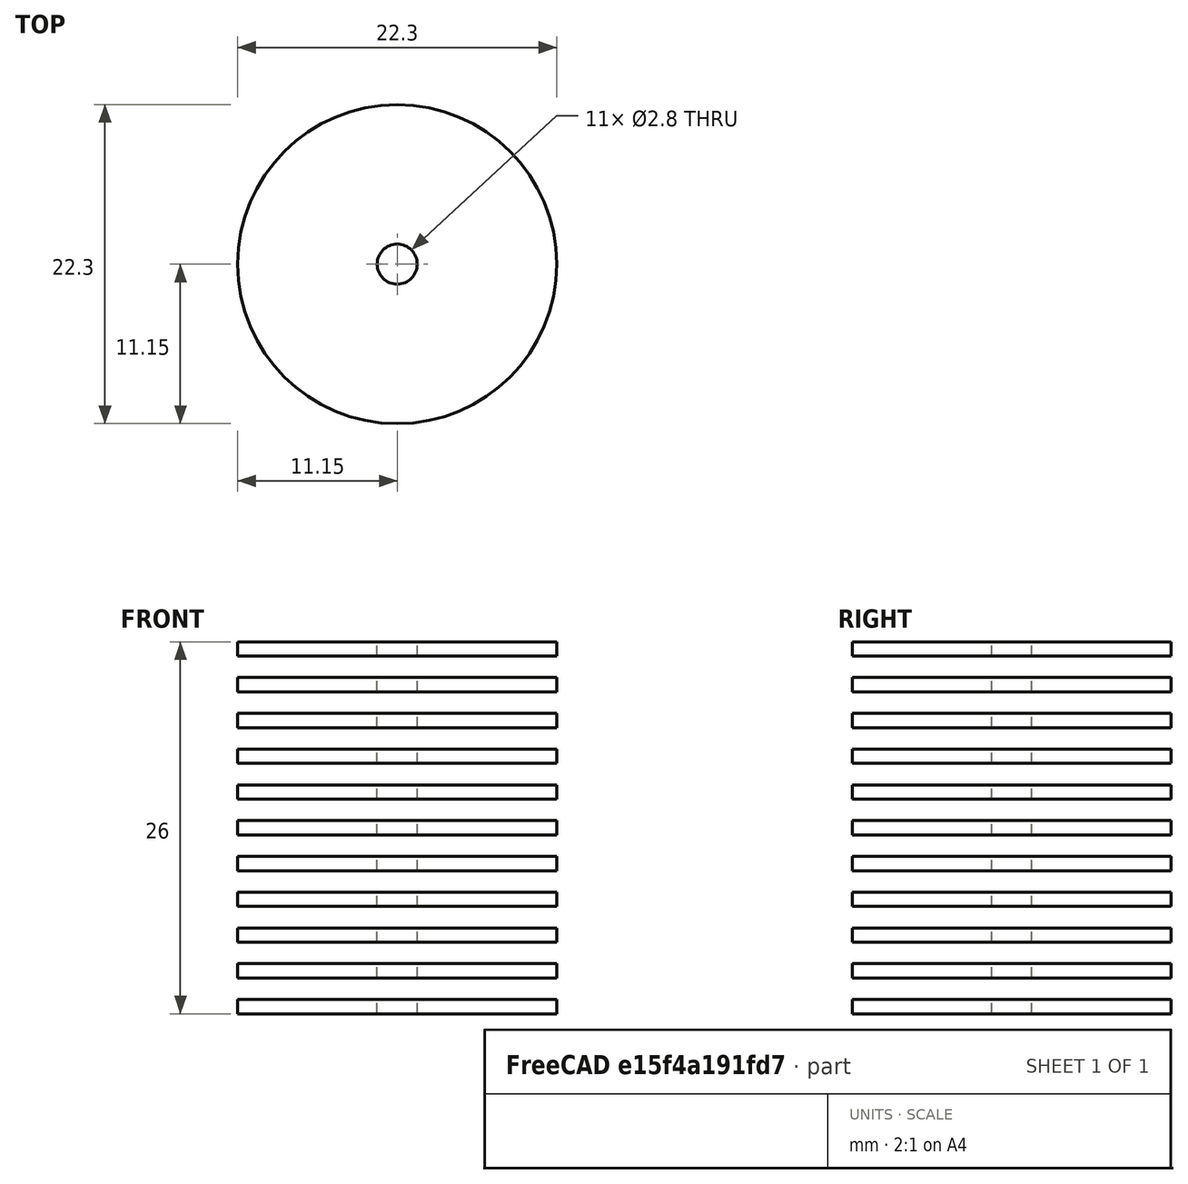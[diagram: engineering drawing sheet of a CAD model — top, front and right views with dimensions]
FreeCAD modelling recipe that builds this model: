
FCSTD DOCUMENT  (FreeCAD 0.15R4671 (Git))
Label: radiador
License: CreativeCommons Attribution-ShareAlike
LicenseURL: http://creativecommons.org/licenses/by-sa/4.0/
objects: Part::Cylinder×2, Part::Cut×1, Part::FeaturePython×1, Part::Feature×1
note: 5 computed .brp shape members not serialized (recipe doc carries the construction recipe); baked Part::Feature solids carry a one-line shape summary decoded from their .brp

FEATURE [Part::Cylinder] Cylinder  label="Cilindro"
  Angle = 360
  Height = 1
  Radius = 11.15
FEATURE [Part::Cylinder] Cylinder001  label="Cilindro001"
  Angle = 360
  Height = 10
  Placement = pos=(0,0,-3) rot=(0,0,1;0rad)
  Radius = 1.4
FEATURE [Part::Cut] Cut
  Base = -> Cylinder
  Tool = -> Cylinder001
FEATURE [Part::FeaturePython] Array  # Draft array (typed FeaturePython)
  Angle = 360
  ArrayType = 0
  Axis = (0,0,1)
  Base = -> Cut
  Center = (0,0,0)
  Fuse = false
  IntervalAxis = (0,0,0)
  IntervalX = (0,0,0)
  IntervalY = (0,0,0)
  IntervalZ = (0,0,2.5)
  NumberPolar = 1
  NumberX = 1
  NumberY = 1
  NumberZ = 11
FEATURE [Part::Feature] Array001  label="radiador"
  shape: bbox 22.3 x 22.3 x 26 mm, 44 faces, 11 solids (baked)
